# Revit family: Water_Heater-Haws_Corporation-Enclosed_Emergency_Environments_8780
name_source: partatom
category: Plumbing Fixtures
revit_build: Autodesk Revit 2018 (Build: 20170223_1515(x64)
units: mm (PartAtom-declared; Revit-internal decimal feet)

## family parameters
Always vertical = Yes
Cut with Voids When Loaded = No
OmniClass Number = 23.65.35.11
Part Type = Normal
Room Calculation Point = No
Round Connector Dimension = Use Diameter
Shared = No
Work Plane-Based = No

## types (1)
- 8780 - Emergency Water Tempering Skid
    Amperage = 20 A
    Apparent Load = 4224 VA
    Assembly Code = G3010500
    BLENDING SYSTEM = Metal - Haws Corporation - Brass
    Bracket = Metal - Haws Corporation - Polished Chrome
    COLD WATER INLET = 14 1/2"
    CW Connection = Yes
    CWFU = 1
    Description = Single or multiple shower and/or eyewash feeder is designed to operate with a number of tempering and electrical options
    Edition number = 1
    Expansion Tank = Metal - Haws Corporation - Polished Chrome
    Flow = 20 GPM
    Full Height = 75"
    Full Length = 60"
    Full Width = 48"
    HW Connection = Yes
    HWFU = 1
    Keynote = 15200
    Manufacturer = Haws Corporation 1455 Kleppe Lane Sparks, NV 89431
    Model = 8780
    Number of Poles = 1
    Power Consumption = 4 kW
    Power Factor = 0.984752
    Product Guid = fce80424-791a-4533-9994-d181b1aada37
    Product data url = https://bimobject.com
    Sanitary Radius = 5/8"
    Skid = Metal - Haws Corporation - Green
    Socket = Metal - Haws Corporation - High Polished Stainless Steel
    Storage Tank = Metal - Haws Corporation - Smokey Pearl
    Supply Radius = 5/8"
    Tubing = Metal - Haws Corporation - Galvanized Steel
    Type Comments = Skid-mounted tempering system which may supply a number of drench systems or eyewash stations
    URL = http://www.hawsco.com
    Vent Connection = No
    Voltage = 208 V
    WFU = 1
    Waste Connection = Yes

## geometry (parser evidence)
native form markers: Blend x27, Sweep x5
no freeform markers — native parametric forms only
